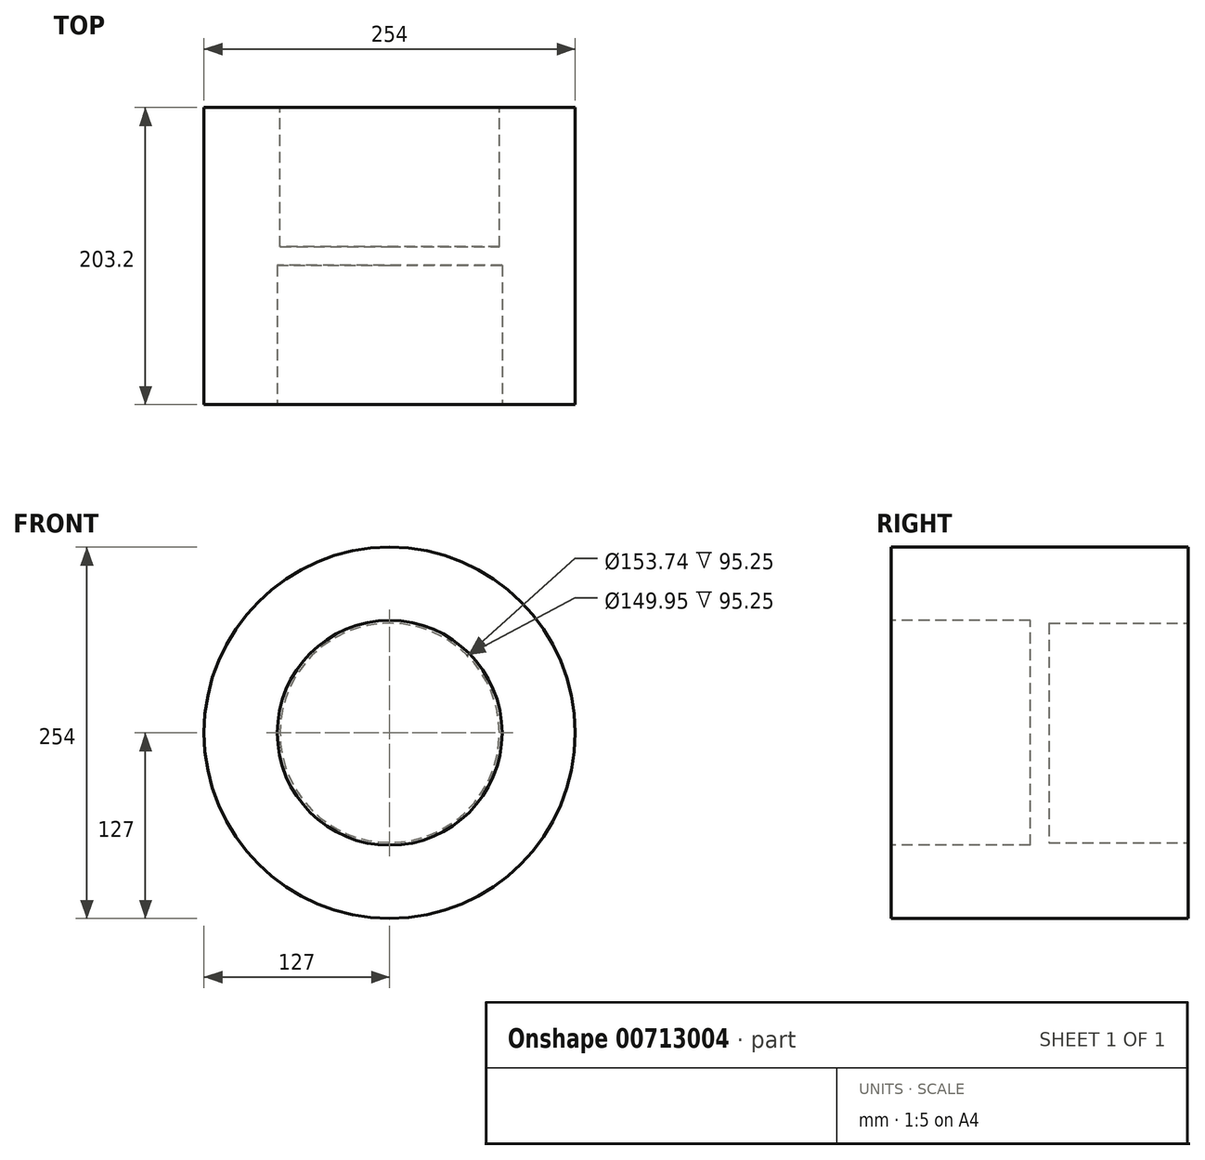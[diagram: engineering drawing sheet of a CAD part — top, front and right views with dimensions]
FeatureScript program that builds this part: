
annotation { "Feature Type Name" : "Feature", "Feature Type Description" : "" }
export const myFeature = defineFeature(function(context is Context, id is Id, definition is map)
    precondition{}
    {
        {
            var Q0;
            Q0=qCreatedBy(makeId("Front.planeOp"),FACE);
            var sketch = newSketch(context, id + "F0", { "sketchPlane" : qUnion([Q0])});
            skCircle(sketch, "E0", {"center": v(0, 0) * mm, "radius": 127 * mm});
            skSolve(sketch);
        }
        {
            var Q0;
            Q0=makeQuery(id+"F0.imprint","IMPRINT",FACE,{"disambiguationData":[TD([[makeQuery(id+"F0.imprint","IMPRINT",EDGE,{"derivedFrom":sQuery(id+"F0.wireOp",EDGE,"E0")}),1.0]])]});
            extrude(context, id + "F1", {"entities" : qUnion([Q0]), "oppositeDirection" : true, "depth" : 203.2 * mm, "offsetDistance" : 25.4 * mm});
        }
        {
            var Q0;
            Q0=makeQuery(id+"F1.opExtrude","CAP_FACE",FACE,{"disambiguationData":[OSD([sQuery(id+"F0.wireOp",EDGE,"E0")])],"isStart":true});
            var sketch = newSketch(context, id + "F2", { "sketchPlane" : qUnion([Q0])});
            skCircle(sketch, "E1", {"center": v(0, 0) * mm, "radius": 76.87 * mm});
            skSolve(sketch);
        }
        {
            var Q0;
            Q0 = qSketchRegion(id + "F2", true);
            extrude(context, id + "F3", {"entities" : qUnion([Q0]), "operationType" : NewBodyOperationType.REMOVE, "oppositeDirection" : true, "depth" : 95.25 * mm, "offsetDistance" : 25.4 * mm});
        }
        {
            var Q0;
            Q0=makeQuery(id+"F1.opExtrude","CAP_FACE",FACE,{"disambiguationData":[OSD([sQuery(id+"F0.wireOp",EDGE,"E0")])],"isStart":false});
            var sketch = newSketch(context, id + "F4", { "sketchPlane" : qUnion([Q0])});
            skCircle(sketch, "E2", {"center": v(0, 0) * mm, "radius": 74.97 * mm});
            skSolve(sketch);
        }
        {
            var Q0;
            Q0=makeQuery(id+"F4.imprint","IMPRINT",FACE,{"disambiguationData":[TD([[makeQuery(id+"F4.imprint","IMPRINT",EDGE,{"derivedFrom":sQuery(id+"F4.wireOp",EDGE,"E2")}),1.0]])]});
            extrude(context, id + "F5", {"entities" : qUnion([Q0]), "operationType" : NewBodyOperationType.REMOVE, "oppositeDirection" : true, "depth" : 95.25 * mm, "offsetDistance" : 25.4 * mm});
        }
    });
